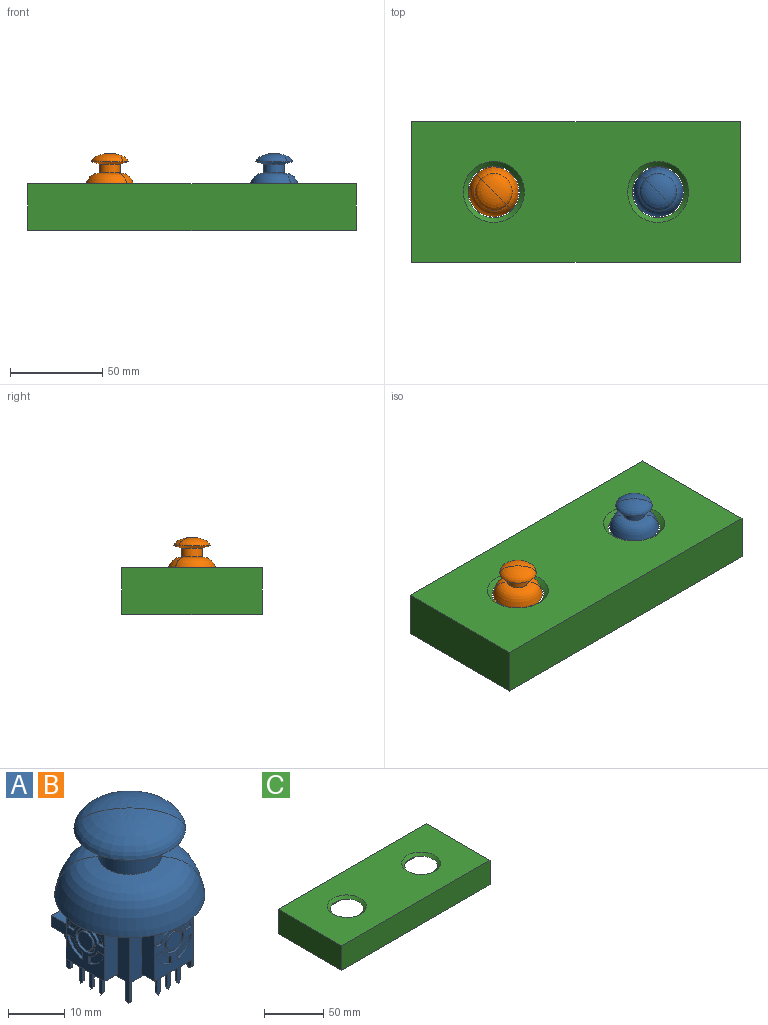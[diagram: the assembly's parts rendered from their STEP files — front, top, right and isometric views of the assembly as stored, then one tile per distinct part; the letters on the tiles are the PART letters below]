
ASSEMBLY  parts=3 mates=5
PART A: 161 faces, bbox 26.7x27.6x34.7 mm
  f0: revolved ~21.88x21.88mm, area 381.7mm2, adj f8,f35,f36
  f1: revolved ~22.76x22.76mm, area 411.4mm2, adj f9,f34,f35
  f2: revolved ~16.91x16.91mm, area 200.7mm2, adj f10,f33
  f3: cylinder r=1.84mm len=3.68mm, axis (0,-1,0), area 5.9mm2, adj f72,f73
  f4: cylinder r=2.41mm len=4.83mm, axis (0,-1,0), area 7.7mm2, adj f66,f72
  f5: cylinder r=1.84mm len=3.68mm, axis (-1,0,0), area 5.9mm2, adj f46,f47
  f6: cylinder r=2.41mm len=4.83mm, axis (-1,0,0), area 7.7mm2, adj f40,f46
  f7: cylinder r=3.11mm len=6.22mm, axis (0,0,-1), area 63.4mm2, adj f8,f16
  f8: cone r=5.08mm half-angle=25.9deg, axis (0,0,1), area 115.8mm2, adj f0,f7,f36
  f9: cylinder r=5.59mm len=11.18mm, axis (0,0,-1), area 169.4mm2, adj f1,f10,f34
  f10: cone r=9.91mm half-angle=73.6deg, axis (0,0,1), area 219.1mm2, adj f2,f9,f33
  f11: cylinder r=1.4mm len=4.32mm, axis (0,-1,0), area 37.9mm2, adj f17,f32
  f12: cylinder r=1.71mm len=3.43mm, axis (0,0,-1), area 19.2mm2, adj f18,f31
  f13: plane 22.23x17.4mm, normal (0,0,-1), area 331.2mm2, adj f14,f15,f17,f20,f21,f22,f23,f24
  f14: plane 15.88x15.88mm, normal (0,-1,0), area 81.7mm2, adj f13,f15,f16,f20,f63,f64,f65,f89
  f15: plane 16.38x15.88mm, normal (-1,0,0), area 86.6mm2, adj f13,f14,f16,f17,f37,f38,f39,f90
  f16: plane 19.05x19.05mm, normal (0,0,1), area 283.7mm2, adj f7,f14,f15,f17,f20,f37,f39,f40
  f17: plane 15.88x15.88mm, normal (0,1,0), area 147.1mm2, adj f11,f13,f15,f16,f18,f19,f20,f21
  f18: plane 6.1x5.33mm, normal (0,0,1), area 23.3mm2, adj f12,f17,f28,f29,f30
  f19: plane 10.92x6.35mm, normal (0,0,1), area 36.8mm2, adj f17,f21,f22,f23,f28,f29,f30
  f20: plane 16.38x15.88mm, normal (1,0,0), area 155mm2, adj f13,f14,f16,f17,f24,f25,f26,f92
  f21: plane 6.35x2.41mm, normal (1,0,0), area 15.3mm2, adj f13,f17,f19,f22
  f22: plane 10.92x2.41mm, normal (0,1,0), area 26.4mm2, adj f13,f19,f21,f23
  f23: plane 6.35x2.41mm, normal (-1,0,0), area 15.3mm2, adj f13,f17,f19,f22
  f24: plane 5.33x1.52mm, normal (0,1,0), area 8.1mm2, adj f13,f20,f25,f27
  f25: plane 8.13x1.52mm, normal (0,0,1), area 12.4mm2, adj f20,f24,f26,f27
  f26: plane 5.33x1.52mm, normal (0,-1,0), area 8.1mm2, adj f13,f20,f25,f27
  f27: plane 8.13x5.33mm, normal (1,0,0), area 43.4mm2, adj f13,f24,f25,f26
  f28: plane 5.33x2.29mm, normal (-1,0,0), area 12.2mm2, adj f17,f18,f19,f30
  f29: plane 5.33x2.29mm, normal (1,0,0), area 12.2mm2, adj f17,f18,f19,f30
  f30: plane 6.1x2.29mm, normal (0,1,0), area 13.9mm2, adj f18,f19,f28,f29
  f31: plane 3.43x3.43mm, normal (0,0,1), area 9.2mm2, adj f12
  f32: plane 2.79x2.79mm, normal (0,1,0), area 6.1mm2, adj f11
  f33: revolved ~16.91x16.91mm, area 200.7mm2, adj f2,f10
  f34: revolved ~22.76x22.76mm, area 411.4mm2, adj f1,f9,f35
  f35: plane 26.67x26.67mm, normal (0,0,-1), area 42.5mm2, adj f0,f1,f34,f36
  f36: revolved ~21.88x21.88mm, area 381.7mm2, adj f0,f8,f35
  f37: plane 11.43x3.18mm, normal (0,1,0), area 36.3mm2, adj f15,f16,f38,f40
  f38: plane 9.78x3.18mm, normal (0,0,-1), area 29.9mm2, adj f15,f37,f39,f40,f119,f122,f123,f124
  f39: plane 11.43x3.18mm, normal (0,-1,0), area 36.3mm2, adj f15,f16,f38,f40
  f40: plane 11.43x9.78mm, normal (-1,0,0), area 66.4mm2, adj f6,f16,f37,f38,f39,f41,f42,f43
  f41: cylinder r=4.57mm len=3.75mm, axis (-1,0,0), area 2.9mm2, adj f40,f42,f44,f45
  f42: plane 1.56x0.51mm, normal (0,-1,0), area 0.8mm2, adj f40,f41,f43,f45
  f43: cylinder r=3.05mm len=2.19mm, axis (-1,0,0), area 1.6mm2, adj f40,f42,f44,f45
  f44: plane 1.56x0.51mm, normal (0,0,-1), area 0.8mm2, adj f40,f41,f43,f45
  f45: plane 3.75x3.75mm, normal (-1,0,0), area 6.8mm2, adj f41,f42,f43,f44
  f46: plane 4.83x4.83mm, normal (-1,0,0), area 7.6mm2, adj f5,f6
  f47: plane 3.68x3.68mm, normal (-1,0,0), area 10.7mm2, adj f5
  f48: cylinder r=4.57mm len=3.75mm, axis (-1,0,0), area 2.9mm2, adj f40,f49,f51,f52
  f49: plane 1.56x0.51mm, normal (0,0,-1), area 0.8mm2, adj f40,f48,f50,f52
  f50: cylinder r=3.05mm len=2.19mm, axis (-1,0,0), area 1.6mm2, adj f40,f49,f51,f52
  f51: plane 1.56x0.51mm, normal (0,1,0), area 0.8mm2, adj f40,f48,f50,f52
  f52: plane 3.75x3.75mm, normal (-1,0,0), area 6.8mm2, adj f48,f49,f50,f51
  f53: cylinder r=4.57mm len=3.75mm, axis (-1,0,0), area 2.9mm2, adj f40,f54,f56,f57
  f54: plane 1.56x0.51mm, normal (0,1,0), area 0.8mm2, adj f40,f53,f55,f57
  f55: cylinder r=3.05mm len=2.19mm, axis (-1,0,0), area 1.6mm2, adj f40,f54,f56,f57
  f56: plane 1.56x0.51mm, normal (0,0,1), area 0.8mm2, adj f40,f53,f55,f57
  f57: plane 3.75x3.75mm, normal (-1,0,0), area 6.8mm2, adj f53,f54,f55,f56
  f58: cylinder r=4.57mm len=3.75mm, axis (-1,0,0), area 2.9mm2, adj f40,f59,f61,f62
  f59: plane 1.56x0.51mm, normal (0,0,1), area 0.8mm2, adj f40,f58,f60,f62
  f60: cylinder r=3.05mm len=2.19mm, axis (-1,0,0), area 1.6mm2, adj f40,f59,f61,f62
  f61: plane 1.56x0.51mm, normal (0,-1,0), area 0.8mm2, adj f40,f58,f60,f62
  f62: plane 3.75x3.75mm, normal (-1,0,0), area 6.8mm2, adj f58,f59,f60,f61
  f63: plane 11.43x3.18mm, normal (-1,0,0), area 36.3mm2, adj f14,f16,f64,f66
  f64: plane 9.78x3.18mm, normal (0,0,-1), area 29.9mm2, adj f14,f63,f65,f66,f103,f104,f105,f106
  f65: plane 11.43x3.18mm, normal (1,0,0), area 36.3mm2, adj f14,f16,f64,f66
  f66: plane 11.43x9.78mm, normal (0,-1,0), area 66.4mm2, adj f4,f16,f63,f64,f65,f67,f68,f69
  f67: cylinder r=4.57mm len=3.75mm, axis (0,-1,0), area 2.9mm2, adj f66,f68,f70,f71
  f68: plane 1.56x0.51mm, normal (1,0,0), area 0.8mm2, adj f66,f67,f69,f71
  f69: cylinder r=3.05mm len=2.19mm, axis (0,-1,0), area 1.6mm2, adj f66,f68,f70,f71
  f70: plane 1.56x0.51mm, normal (0,0,-1), area 0.8mm2, adj f66,f67,f69,f71
  f71: plane 3.75x3.75mm, normal (0,-1,0), area 6.8mm2, adj f67,f68,f69,f70
  f72: plane 4.83x4.83mm, normal (0,-1,0), area 7.6mm2, adj f3,f4
  f73: plane 3.68x3.68mm, normal (0,-1,0), area 10.7mm2, adj f3
  f74: cylinder r=4.57mm len=3.75mm, axis (0,-1,0), area 2.9mm2, adj f66,f75,f77,f78
  f75: plane 1.56x0.51mm, normal (0,0,-1), area 0.8mm2, adj f66,f74,f76,f78
  f76: cylinder r=3.05mm len=2.19mm, axis (0,-1,0), area 1.6mm2, adj f66,f75,f77,f78
  f77: plane 1.56x0.51mm, normal (-1,0,0), area 0.8mm2, adj f66,f74,f76,f78
  f78: plane 3.75x3.75mm, normal (0,-1,0), area 6.8mm2, adj f74,f75,f76,f77
  f79: cylinder r=4.57mm len=3.75mm, axis (0,-1,0), area 2.9mm2, adj f66,f80,f82,f83
  f80: plane 1.56x0.51mm, normal (-1,0,0), area 0.8mm2, adj f66,f79,f81,f83
  f81: cylinder r=3.05mm len=2.19mm, axis (0,-1,0), area 1.6mm2, adj f66,f80,f82,f83
  f82: plane 1.56x0.51mm, normal (0,0,1), area 0.8mm2, adj f66,f79,f81,f83
  f83: plane 3.75x3.75mm, normal (0,-1,0), area 6.8mm2, adj f79,f80,f81,f82
  f84: cylinder r=4.57mm len=3.75mm, axis (0,-1,0), area 2.9mm2, adj f66,f85,f87,f88
  f85: plane 1.56x0.51mm, normal (0,0,1), area 0.8mm2, adj f66,f84,f86,f88
  f86: cylinder r=3.05mm len=2.19mm, axis (0,-1,0), area 1.6mm2, adj f66,f85,f87,f88
  f87: plane 1.56x0.51mm, normal (1,0,0), area 0.8mm2, adj f66,f84,f86,f88
  f88: plane 3.75x3.75mm, normal (0,-1,0), area 6.8mm2, adj f84,f85,f86,f87
  f89: plane 4.45x1.02mm, normal (1,0,0), area 4.4mm2, adj f13,f14,f90,f97
  f90: plane 3.94x0.51mm, normal (0,1,0), area 2mm2, adj f13,f15,f89,f97
  f91: plane 4.45x1.02mm, normal (-1,0,0), area 4.4mm2, adj f13,f14,f92,f100
  f92: plane 3.94x0.51mm, normal (0,1,0), area 2mm2, adj f13,f20,f91,f100
  f93: plane 4.45x1.02mm, normal (1,0,0), area 4.4mm2, adj f13,f17,f94,f98
  f94: plane 3.94x0.51mm, normal (0,-1,0), area 2mm2, adj f13,f15,f93,f98
  f95: plane 4.45x1.02mm, normal (-1,0,0), area 4.4mm2, adj f13,f17,f96,f99
  f96: plane 3.94x0.51mm, normal (0,-1,0), area 2mm2, adj f13,f20,f95,f99
  f97: cylinder r=0.51mm len=1.02mm, axis (-1,0,0), area 0.8mm2, adj f14,f15,f89,f90
  f98: cylinder r=0.51mm len=1.02mm, axis (-1,0,0), area 0.8mm2, adj f15,f17,f93,f94
  f99: cylinder r=0.51mm len=1.02mm, axis (-1,0,0), area 0.8mm2, adj f17,f20,f95,f96
  f100: cylinder r=0.51mm len=1.02mm, axis (-1,0,0), area 0.8mm2, adj f14,f20,f91,f92
  f101: plane 0.6x0.51mm, normal (-0.84,0,-0.54), area 0.4mm2, adj f102,f104,f105,f106
  f102: plane 0.6x0.51mm, normal (0.84,0,-0.54), area 0.4mm2, adj f101,f103,f105,f106
  f103: plane 4.21x0.51mm, normal (1,0,0), area 2.1mm2, adj f64,f102,f105,f106
  f104: plane 4.21x0.51mm, normal (-1,0,0), area 2.1mm2, adj f64,f101,f105,f106
  f105: plane 4.81x0.76mm, normal (0,-1,0), area 3.4mm2, adj f64,f101,f102,f103,f104
  f106: plane 4.81x0.76mm, normal (0,1,0), area 3.4mm2, adj f64,f101,f102,f103,f104
  f107: plane 4.21x0.51mm, normal (-1,0,0), area 2.1mm2, adj f64,f108,f111,f112
  f108: plane 0.6x0.51mm, normal (-0.84,0,-0.54), area 0.4mm2, adj f107,f109,f111,f112
  f109: plane 0.6x0.51mm, normal (0.84,0,-0.54), area 0.4mm2, adj f108,f110,f111,f112
  f110: plane 4.21x0.51mm, normal (1,0,0), area 2.1mm2, adj f64,f109,f111,f112
  f111: plane 4.81x0.76mm, normal (0,-1,0), area 3.4mm2, adj f64,f107,f108,f109,f110
  f112: plane 4.81x0.76mm, normal (0,1,0), area 3.4mm2, adj f64,f107,f108,f109,f110
  f113: plane 4.21x0.51mm, normal (-1,0,0), area 2.1mm2, adj f64,f114,f117,f118
  f114: plane 0.6x0.51mm, normal (-0.84,0,-0.54), area 0.4mm2, adj f113,f115,f117,f118
  f115: plane 0.6x0.51mm, normal (0.84,0,-0.54), area 0.4mm2, adj f114,f116,f117,f118
  f116: plane 4.21x0.51mm, normal (1,0,0), area 2.1mm2, adj f64,f115,f117,f118
  f117: plane 4.81x0.76mm, normal (0,-1,0), area 3.4mm2, adj f64,f113,f114,f115,f116
  f118: plane 4.81x0.76mm, normal (0,1,0), area 3.4mm2, adj f64,f113,f114,f115,f116
  f119: plane 4.21x0.51mm, normal (0,1,0), area 2.1mm2, adj f38,f120,f123,f124
  f120: plane 0.6x0.51mm, normal (0,0.84,-0.54), area 0.4mm2, adj f119,f121,f123,f124
  f121: plane 0.6x0.51mm, normal (0,-0.84,-0.54), area 0.4mm2, adj f120,f122,f123,f124
  f122: plane 4.21x0.51mm, normal (0,-1,0), area 2.1mm2, adj f38,f121,f123,f124
  f123: plane 4.81x0.76mm, normal (-1,0,0), area 3.4mm2, adj f38,f119,f120,f121,f122
  f124: plane 4.81x0.76mm, normal (1,0,0), area 3.4mm2, adj f38,f119,f120,f121,f122
  f125: plane 4.21x0.51mm, normal (0,1,0), area 2.1mm2, adj f38,f126,f129,f130
  f126: plane 0.6x0.51mm, normal (0,0.84,-0.54), area 0.4mm2, adj f125,f127,f129,f130
  f127: plane 0.6x0.51mm, normal (0,-0.84,-0.54), area 0.4mm2, adj f126,f128,f129,f130
  f128: plane 4.21x0.51mm, normal (0,-1,0), area 2.1mm2, adj f38,f127,f129,f130
  f129: plane 4.81x0.76mm, normal (-1,0,0), area 3.4mm2, adj f38,f125,f126,f127,f128
  f130: plane 4.81x0.76mm, normal (1,0,0), area 3.4mm2, adj f38,f125,f126,f127,f128
  f131: plane 4.21x0.51mm, normal (0,1,0), area 2.1mm2, adj f38,f132,f135,f136
  f132: plane 0.6x0.51mm, normal (0,0.84,-0.54), area 0.4mm2, adj f131,f133,f135,f136
  f133: plane 0.6x0.51mm, normal (0,-0.84,-0.54), area 0.4mm2, adj f132,f134,f135,f136
  f134: plane 4.21x0.51mm, normal (0,-1,0), area 2.1mm2, adj f38,f133,f135,f136
  f135: plane 4.81x0.76mm, normal (-1,0,0), area 3.4mm2, adj f38,f131,f132,f133,f134
  f136: plane 4.81x0.76mm, normal (1,0,0), area 3.4mm2, adj f38,f131,f132,f133,f134
  f137: plane 2.54x0.51mm, normal (1,0,0), area 1.2mm2, adj f13,f138,f140,f159,f160
  f138: plane 2.29x0.25mm, normal (0,-1,0), area 0.6mm2, adj f13,f137,f139,f160
  f139: plane 2.54x0.51mm, normal (-1,0,0), area 1.2mm2, adj f13,f138,f140,f159,f160
  f140: plane 2.29x0.25mm, normal (0,1,0), area 0.6mm2, adj f13,f137,f139,f159
  f141: plane 2.54x0.51mm, normal (1,0,0), area 1.2mm2, adj f13,f142,f144,f157,f158
  f142: plane 2.29x0.25mm, normal (0,-1,0), area 0.6mm2, adj f13,f141,f143,f158
  f143: plane 2.54x0.51mm, normal (-1,0,0), area 1.2mm2, adj f13,f142,f144,f157,f158
  f144: plane 2.29x0.25mm, normal (0,1,0), area 0.6mm2, adj f13,f141,f143,f157
  f145: plane 2.54x0.51mm, normal (1,0,0), area 1.2mm2, adj f13,f146,f148,f155,f156
  f146: plane 2.29x0.25mm, normal (0,-1,0), area 0.6mm2, adj f13,f145,f147,f156
  f147: plane 2.54x0.51mm, normal (-1,0,0), area 1.2mm2, adj f13,f146,f148,f155,f156
  f148: plane 2.29x0.25mm, normal (0,1,0), area 0.6mm2, adj f13,f145,f147,f155
  f149: plane 2.54x0.51mm, normal (1,0,0), area 1.2mm2, adj f13,f150,f152,f153,f154
  f150: plane 2.29x0.25mm, normal (0,-1,0), area 0.6mm2, adj f13,f149,f151,f154
  f151: plane 2.54x0.51mm, normal (-1,0,0), area 1.2mm2, adj f13,f150,f152,f153,f154
  f152: plane 2.29x0.25mm, normal (0,1,0), area 0.6mm2, adj f13,f149,f151,f153
  f153: plane 0.25x0.25mm, normal (0,0.71,-0.71), area 0.1mm2, adj f149,f151,f152,f154
  f154: plane 0.25x0.25mm, normal (0,-0.71,-0.71), area 0.1mm2, adj f149,f150,f151,f153
  f155: plane 0.25x0.25mm, normal (0,0.71,-0.71), area 0.1mm2, adj f145,f147,f148,f156
  f156: plane 0.25x0.25mm, normal (0,-0.71,-0.71), area 0.1mm2, adj f145,f146,f147,f155
  f157: plane 0.25x0.25mm, normal (0,0.71,-0.71), area 0.1mm2, adj f141,f143,f144,f158
  f158: plane 0.25x0.25mm, normal (0,-0.71,-0.71), area 0.1mm2, adj f141,f142,f143,f157
  f159: plane 0.25x0.25mm, normal (0,0.71,-0.71), area 0.1mm2, adj f137,f139,f140,f160
  f160: plane 0.25x0.25mm, normal (0,-0.71,-0.71), area 0.1mm2, adj f137,f138,f139,f159
PART B: same geometry as A
PART C: 13 faces, bbox 177.8x76.2x25.4 mm
  f0: plane 177.8x76.2mm, normal (0,0,-1), area 1264.5mm2, adj f1,f2,f3,f4,f6,f7,f8,f9
  f1: plane 76.2x25.4mm, normal (1,0,0), area 1935.5mm2, adj f0,f2,f4,f5
  f2: plane 177.8x25.4mm, normal (0,1,0), area 4516.1mm2, adj f0,f1,f3,f5
  f3: plane 76.2x25.4mm, normal (-1,0,0), area 1935.5mm2, adj f0,f2,f4,f5
  f4: plane 177.8x25.4mm, normal (0,-1,0), area 4516.1mm2, adj f0,f1,f3,f5
  f5: plane 177.8x76.2mm, normal (0,0,1), area 11835.7mm2, adj f1,f2,f3,f4,f11,f12
  f6: plane 71.12x22.86mm, normal (-1,0,0), area 1625.8mm2, adj f0,f7,f9,f10
  f7: plane 172.72x22.86mm, normal (0,-1,0), area 3948.4mm2, adj f0,f6,f8,f10
  f8: plane 71.12x22.86mm, normal (1,0,0), area 1625.8mm2, adj f0,f7,f9,f10
  f9: plane 172.72x22.86mm, normal (0,1,0), area 3948.4mm2, adj f0,f6,f8,f10
  f10: plane 172.72x71.12mm, normal (0,0,-1), area 11057.6mm2, adj f6,f7,f8,f9,f11,f12
  f11: cone r=13.97mm half-angle=45deg, axis (0,0,1), area 344mm2, adj f5,f10
  f12: cone r=13.97mm half-angle=45deg, axis (0,0,1), area 344mm2, adj f5,f10
PLACE A t=(-37.61,2.08,-35.08)mm
PLACE B t=(-126.51,2.08,-35.08)mm
PLACE C t=(-74.12,10.02,-46.51)mm fixed
MATE cylindrical A.f7 <-> C.f11  axis (0,0,-1) through (-29.67,10.02,-23.65)mm
MATE planar B.f17 <-> A.f17  axis (0,1,0) through (-126.51,17.96,-31.08)mm
MATE planar C.f10 <-> A.f7  axis (0,0,-1) through (-74.12,10.02,-23.65)mm
MATE cylindrical B.f7 <-> C.f12  axis (0,0,-1) through (-118.57,10.02,-23.65)mm
MATE planar B.f13 <-> A.f13  axis (0,0,-1) through (-118.25,12.33,-35.08)mm
